# Revit family: SILENTLAB CUBIQ
name_source: partatom
category: Furniture Systems
revit_build: Autodesk Revit 2017 (Build: 20190508_0315(x64)
units: mm (PartAtom-declared; Revit-internal decimal feet)

## family parameters
Always vertical = Yes
Cut with Voids When Loaded = No
OmniClass Number = 23.40.70.14.64.21.14
OmniClass Title = Free-Standing Component
Part Type = Normal
Room Calculation Point = No
Round Connector Dimension = Use Diameter
Shared = No
Work Plane-Based = No

## types (1)
- default
    Height = 2270 mm
    Leg Height = 40 mm
    Length = 1500 mm  [stored 4.92126 ft]
    Light ON = Yes
    Material = SilentLab - Plátno
    Material Carpet = SilentLab - Koberec
    Material Frame = SilentLab - Dřevo
    Material Glass = SilentLab - Sklo
    Material of fitting = SilentLab - Ocel
    Panel Height = 339 mm
    Width = 1780 mm

note: [stored X ft] marks values corroborated as IEEE doubles in the binary element streams (Revit-internal decimal feet)

## geometry (parser evidence)
native form markers: Sweep x3
no freeform markers — native parametric forms only
